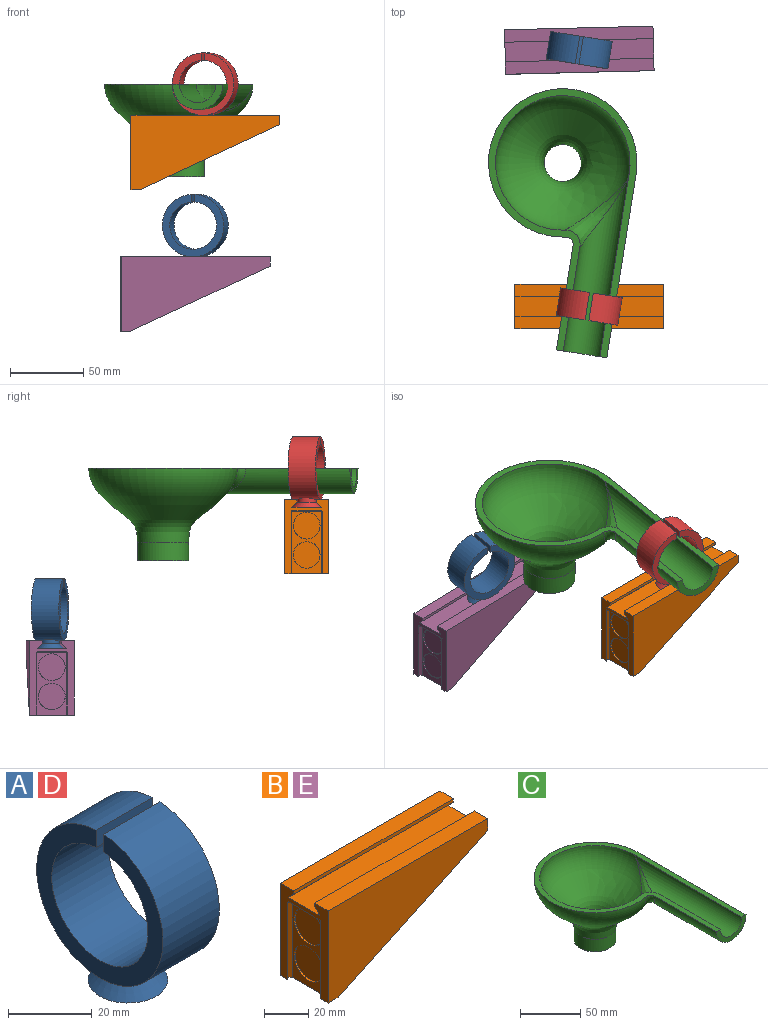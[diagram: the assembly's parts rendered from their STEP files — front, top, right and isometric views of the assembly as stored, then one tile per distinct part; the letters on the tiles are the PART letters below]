
ASSEMBLY  parts=5 mates=3
PART A: 9 faces, bbox 19.1x42.7x48 mm
  f0: cylinder r=6.35mm len=12.7mm, axis (0,0,-1), area 107.3mm2, adj f1,f5
  f1: cone r=6.35mm half-angle=45deg, axis (0,0,-1), area 223.9mm2, adj f0,f2
  f2: plane 19.05x19.05mm, normal (0,0,-1), area 285mm2, adj f1
  f3: cylinder r=16.26mm len=32.51mm, axis (-1,0,0), area 1897.3mm2, adj f4,f6,f7,f8
  f4: plane 19.05x5.09mm, normal (0,1,0), area 97mm2, adj f3,f5,f7,f8
  f5: cylinder r=21.34mm len=42.67mm, axis (-1,0,0), area 2377.4mm2, adj f0,f4,f6,f7,f8
  f6: plane 19.05x5.09mm, normal (0,-1,0), area 97mm2, adj f3,f5,f7,f8
  f7: plane 42.67x42.63mm, normal (1,0,0), area 587mm2, adj f3,f4,f5,f6
  f8: plane 42.67x42.63mm, normal (-1,0,0), area 587mm2, adj f3,f4,f5,f6
PART B: 29 faces, bbox 101.6x30.4x50.8 mm
  f0: plane 23.58x2.79mm, normal (0,0,-1), area 7.1mm2, adj f11,f14,f15,f16,f17,f18,f23,f24
  f1: plane 30.44x6.35mm, normal (0,0,-1), area 131.3mm2, adj f5,f6,f11,f13,f14,f15,f16,f17
  f2: plane 101.6x3.43mm, normal (0,0.71,-0.71), area 492.7mm2, adj f3,f10,f11,f12
  f3: plane 101.6x1.91mm, normal (0,1,0), area 193.5mm2, adj f2,f4,f11,f12
  f4: plane 101.6x8.51mm, normal (0,0,1), area 864.5mm2, adj f3,f5,f11,f12
  f5: plane 101.6x50.8mm, normal (0,-1,0), area 3044.3mm2, adj f1,f4,f11,f12,f13
  f6: plane 101.6x50.8mm, normal (0,1,0), area 3044.3mm2, adj f1,f7,f11,f12,f13
  f7: plane 101.6x8.51mm, normal (0,0,1), area 864.5mm2, adj f6,f8,f11,f12
  f8: plane 101.6x1.91mm, normal (0,-1,0), area 193.5mm2, adj f7,f9,f11,f12
  f9: plane 101.6x3.43mm, normal (0,-0.71,-0.71), area 492.7mm2, adj f8,f10,f11,f12
  f10: plane 101.6x20.28mm, normal (0,0,1), area 2060.1mm2, adj f2,f9,f11,f12
  f11: plane 50.8x30.44mm, normal (-1,0,0), area 554.8mm2, adj f0,f1,f2,f3,f4,f5,f6,f7
  f12: plane 30.44x6.35mm, normal (1,0,0), area 109.9mm2, adj f2,f3,f4,f5,f6,f7,f8,f9
  f13: plane 95.25x44.45mm, normal (0.42,0,-0.91), area 3199.2mm2, adj f1,f5,f6,f12
  f14: plane 42.67x20.53mm, normal (-1,0,0), area 350.7mm2, adj f0,f1,f16,f17,f20,f22
  f15: plane 42.67x1.27mm, normal (0.71,-0.71,0), area 76.6mm2, adj f0,f1,f11,f16
  f16: plane 42.67x1.52mm, normal (-0.71,-0.71,0), area 92mm2, adj f0,f1,f14,f15
  f17: plane 42.67x1.52mm, normal (-0.71,0.71,0), area 92mm2, adj f0,f1,f14,f18
  f18: plane 42.67x1.27mm, normal (0.71,0.71,0), area 76.6mm2, adj f0,f1,f11,f17
  f19: plane 18.29x18.29mm, normal (-1,0,0), area 262.7mm2, adj f20
  f20: cylinder r=9.14mm len=18.29mm, axis (-1,0,0), area 43.8mm2, adj f14,f19
  f21: plane 18.29x18.29mm, normal (-1,0,0), area 262.7mm2, adj f22
  f22: cylinder r=9.14mm len=18.29mm, axis (-1,0,0), area 43.8mm2, adj f14,f21
  f23: plane 20.32x0.51mm, normal (-1,0,0), area 10.3mm2, adj f0,f24,f27,f28
  f24: plane 1.27x1.27mm, normal (-0.71,0.71,0), area 0.9mm2, adj f0,f23,f25,f28
  f25: plane 1.27x1.27mm, normal (0.71,0.71,0), area 0.9mm2, adj f0,f11,f24,f28
  f26: plane 1.27x1.27mm, normal (0.71,-0.71,0), area 0.9mm2, adj f0,f11,f27,f28
  f27: plane 1.27x1.27mm, normal (-0.71,-0.71,0), area 0.9mm2, adj f0,f23,f26,f28
  f28: plane 22.86x2.54mm, normal (0,0,-1), area 54.8mm2, adj f11,f23,f24,f25,f26,f27
PART C: 11 faces, bbox 102.1x178.3x65 mm
  f0: plane 178.25x102.05mm, normal (0,0,1), area 2142.8mm2, adj f1,f2,f6,f7,f8,f9,f10
  f1: revolved ~92.08x92.08mm, area 10641.1mm2, adj f0,f5,f9
  f2: revolved ~101.6x101.6mm, area 12626.2mm2, adj f0,f4,f10
  f3: plane 34.93x34.93mm, normal (0,0,-1), area 451.3mm2, adj f4,f5
  f4: cylinder r=17.46mm len=34.93mm, axis (0,0,-1), area 1393.4mm2, adj f2,f3
  f5: cylinder r=12.7mm len=25.4mm, axis (0,0,-1), area 1013.4mm2, adj f1,f3
  f6: cylinder r=12.7mm len=127mm, axis (0,-1,0), area 3847.2mm2, adj f0,f7,f9
  f7: plane 34.93x17.46mm, normal (0,-1,0), area 225.6mm2, adj f0,f6,f8
  f8: cylinder r=17.46mm len=127mm, axis (0,-1,0), area 5289.9mm2, adj f0,f7,f10
  f9: bspline ~54.83x37.14mm, area 336.8mm2, adj f0,f1,f6
  f10: bspline ~54.83x40.99mm, area 219.4mm2, adj f0,f2,f8
PART D: same geometry as A
PART E: same geometry as B
PLACE A rot(axis=(0,0,1),80.9deg) t=(-84.96,195.64,-60.32)mm
PLACE B t=(98.04,127,36.77)mm
PLACE C rot(axis=(0,0,-1),9.1deg) t=(29.15,98.32,-11.38)mm
PLACE D rot(axis=(0,0,-1),99.1deg) t=(172.66,-19.99,36.51)mm
PLACE E rot(axis=(0,0,1),1.4deg) t=(88.13,303.86,-60.07)mm
MATE slider C.f6 <-> D.f3  axis (-0.16,-0.99,0) through (42.09,-32.34,39.42)mm
MATE revolute B.f10 <-> D.f0  axis (0,0,1) through (47.24,0,12.7)mm
MATE revolute E.f10 <-> A.f0  axis (0,0,1) through (40.46,175.65,-84.14)mm
